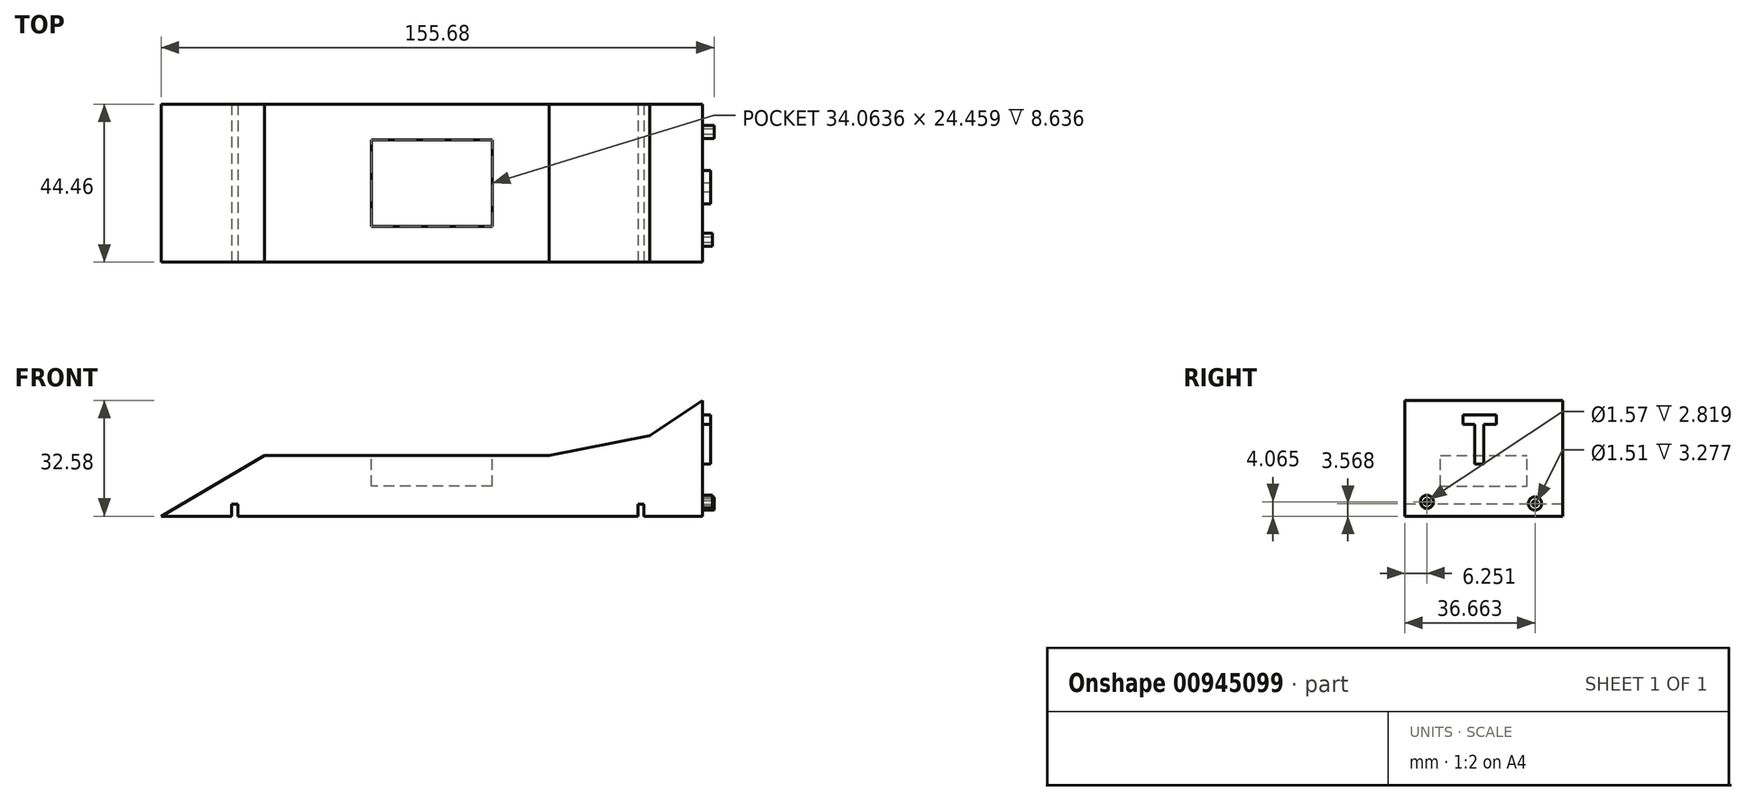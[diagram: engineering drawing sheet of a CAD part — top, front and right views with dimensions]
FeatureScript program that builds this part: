
annotation { "Feature Type Name" : "Feature", "Feature Type Description" : "" }
export const myFeature = defineFeature(function(context is Context, id is Id, definition is map)
    precondition{}
    {
        {
            var Q0;
            Q0=qCreatedBy(makeId("Top.planeOp"),FACE);
            var sketch = newSketch(context, id + "F0", { "sketchPlane" : qUnion([Q0])});
            skLineSegment(sketch, "E0.bottom", {"start": v(76.2, -22.22) * mm, "end": v(-76.2, -22.23) * mm});
            skLineSegment(sketch, "E0.top", {"start": v(76.2, 22.23) * mm, "end": v(-76.2, 22.22) * mm});
            skLineSegment(sketch, "E0.left", {"start": v(76.2, -22.22) * mm, "end": v(76.2, 22.23) * mm});
            skLineSegment(sketch, "E0.right", {"start": v(-76.2, -22.23) * mm, "end": v(-76.2, 22.22) * mm});
            skPoint(sketch, "E0.middle", {"position": v(0, 0) * mm});
            skSolve(sketch);
        }
        {
            var Q0;
            Q0 = qSketchRegion(id + "F0", true);
            extrude(context, id + "F1", {"entities" : qUnion([Q0]), "depth" : 38.1 * mm, "offsetDistance" : 25.4 * mm});
        }
        {
            var Q0;
            Q0=makeQuery(id+"F1.opExtrude","SWEPT_FACE",FACE,{"disambiguationData":[OSD([sQuery(id+"F0.wireOp",EDGE,"E0.bottom")])]});
            var sketch = newSketch(context, id + "F2", { "sketchPlane" : qUnion([Q0])});
            skLineSegment(sketch, "E1", {"start": v(-76.2, 0) * mm, "end": v(-47.13, 17.13) * mm});
            skLineSegment(sketch, "E2", {"start": v(-47.13, 17.13) * mm, "end": v(33.07, 17.13) * mm});
            skLineSegment(sketch, "E3", {"start": v(33.07, 17.13) * mm, "end": v(61.4, 22.68) * mm});
            skLineSegment(sketch, "E4", {"start": v(61.4, 22.68) * mm, "end": v(76.2, 32.58) * mm});
            skLineSegment(sketch, "E5", {"start": v(76.2, 32.58) * mm, "end": v(86.74, 41.3) * mm});
            skLineSegment(sketch, "E6", {"start": v(86.74, 41.3) * mm, "end": v(-31.3, 57.73) * mm});
            skLineSegment(sketch, "E7", {"start": v(-31.3, 57.73) * mm, "end": v(-92.1, 33.96) * mm});
            skLineSegment(sketch, "E8", {"start": v(-92.1, 33.96) * mm, "end": v(-76.2, 0) * mm});
            skSolve(sketch);
        }
        {
            var Q0;
            Q0 = qSketchRegion(id + "F2", true);
            extrude(context, id + "F3", {"entities" : qUnion([Q0]), "operationType" : NewBodyOperationType.REMOVE, "oppositeDirection" : true, "depth" : 87.38 * mm, "offsetDistance" : 25.4 * mm});
        }
        {
            var Q0;
            Q0=makeQuery(id+"F3.boolean.opBoolean","COPY",FACE,{"derivedFrom":makeQuery(id+"F3.opExtrude","SWEPT_FACE",FACE,{"disambiguationData":[OSD([sQuery(id+"F2.wireOp",EDGE,"E2")])]})});
            var sketch = newSketch(context, id + "F4", { "sketchPlane" : qUnion([Q0])});
            skLineSegment(sketch, "E9.bottom", {"start": v(17.03, -12.23) * mm, "end": v(-17.03, -12.23) * mm});
            skLineSegment(sketch, "E9.top", {"start": v(17.03, 12.23) * mm, "end": v(-17.03, 12.23) * mm});
            skLineSegment(sketch, "E9.left", {"start": v(17.03, -12.23) * mm, "end": v(17.03, 12.23) * mm});
            skLineSegment(sketch, "E9.right", {"start": v(-17.03, -12.23) * mm, "end": v(-17.03, 12.23) * mm});
            skPoint(sketch, "E9.middle", {"position": v(0, 0) * mm});
            skSolve(sketch);
        }
        {
            var Q0;
            Q0 = qSketchRegion(id + "F4", true);
            extrude(context, id + "F5", {"entities" : qUnion([Q0]), "operationType" : NewBodyOperationType.REMOVE, "oppositeDirection" : true, "depth" : 8.64 * mm, "offsetDistance" : 25.4 * mm});
        }
        {
            var Q0;
            Q0=makeQuery(id+"F1.opExtrude","SWEPT_FACE",FACE,{"disambiguationData":[OSD([sQuery(id+"F0.wireOp",EDGE,"E0.bottom")])]});
            var sketch = newSketch(context, id + "F6", { "sketchPlane" : qUnion([Q0])});
            skLineSegment(sketch, "E10.bottom", {"start": v(-56.32, 3.35) * mm, "end": v(-54.56, 3.35) * mm});
            skLineSegment(sketch, "E10.top", {"start": v(-56.32, -9.1) * mm, "end": v(-54.56, -9.1) * mm});
            skLineSegment(sketch, "E10.left", {"start": v(-56.32, 3.35) * mm, "end": v(-56.32, -9.1) * mm});
            skLineSegment(sketch, "E10.right", {"start": v(-54.56, 3.35) * mm, "end": v(-54.56, -9.1) * mm});
            skSolve(sketch);
        }
        {
            var Q0;
            Q0 = qSketchRegion(id + "F6", true);
            extrude(context, id + "F7", {"entities" : qUnion([Q0]), "operationType" : NewBodyOperationType.REMOVE, "oppositeDirection" : true, "depth" : 71.12 * mm, "offsetDistance" : 25.4 * mm});
        }
        {
            var Q0;
            Q0=makeQuery(id+"F1.opExtrude","SWEPT_FACE",FACE,{"disambiguationData":[OSD([sQuery(id+"F0.wireOp",EDGE,"E0.bottom")])]});
            var sketch = newSketch(context, id + "F8", { "sketchPlane" : qUnion([Q0])});
            skLineSegment(sketch, "E11.bottom", {"start": v(58.03, 3.35) * mm, "end": v(59.78, 3.35) * mm});
            skLineSegment(sketch, "E11.top", {"start": v(58.03, -2.18) * mm, "end": v(59.78, -2.18) * mm});
            skLineSegment(sketch, "E11.left", {"start": v(58.03, 3.35) * mm, "end": v(58.03, -2.18) * mm});
            skLineSegment(sketch, "E11.right", {"start": v(59.78, 3.35) * mm, "end": v(59.78, -2.18) * mm});
            skSolve(sketch);
        }
        {
            var Q0;
            Q0 = qSketchRegion(id + "F8", true);
            extrude(context, id + "F9", {"entities" : qUnion([Q0]), "operationType" : NewBodyOperationType.REMOVE, "oppositeDirection" : true, "depth" : 63.3 * mm, "offsetDistance" : 25.4 * mm});
        }
        {
            var Q0;
            Q0=makeQuery(id+"F1.opExtrude","SWEPT_FACE",FACE,{"disambiguationData":[OSD([sQuery(id+"F0.wireOp",EDGE,"E0.left")])]});
            var sketch = newSketch(context, id + "F10", { "sketchPlane" : qUnion([Q0])});
            skCircle(sketch, "E12", {"center": v(-15.98, 4.07) * mm, "radius": 0.78 * mm});
            skCircle(sketch, "E13", {"center": v(-15.98, 4.07) * mm, "radius": 1.85 * mm});
            skSolve(sketch);
        }
        {
            var Q0;
            Q0 = qSketchRegion(id + "F10", true);
            extrude(context, id + "F11", {"entities" : qUnion([Q0]), "operationType" : NewBodyOperationType.ADD, "depth" : 2.82 * mm, "offsetDistance" : 25.4 * mm});
        }
        {
            var Q0;
            {var subQ1=sQuery(id+"F0.wireOp",EDGE,"E0.left");var subQ2=sQuery(id+"F0.wireOp",EDGE,"E0.bottom");Q0=makeQuery(id+"F11.boolean.opBoolean","SPLIT",FACE,{"disambiguationData":[TD([makeQuery(id+"F1.opExtrude","SWEPT_FACE",FACE,{"disambiguationData":[OSD([subQ2])]})])],"derivedFrom":makeQuery(id+"F1.opExtrude","SWEPT_FACE",FACE,{"disambiguationData":[OSD([subQ1])]})});}
            var sketch = newSketch(context, id + "F12", { "sketchPlane" : qUnion([Q0])});
            skCircle(sketch, "E14", {"center": v(14.43, 3.57) * mm, "radius": 0.76 * mm});
            skCircle(sketch, "E15", {"center": v(14.43, 3.57) * mm, "radius": 1.87 * mm});
            skSolve(sketch);
        }
        {
            var Q0;
            Q0 = qSketchRegion(id + "F12", true);
            extrude(context, id + "F13", {"entities" : qUnion([Q0]), "operationType" : NewBodyOperationType.ADD, "depth" : 3.28 * mm, "offsetDistance" : 25.4 * mm});
        }
        {
            var Q0;
            {var subQ4=sQuery(id+"F0.wireOp",EDGE,"E0.left");var subQ5=sQuery(id+"F0.wireOp",EDGE,"E0.bottom");var subQ7=makeQuery(id+"F1.opExtrude","SWEPT_FACE",FACE,{"disambiguationData":[OSD([subQ5])]});Q0=makeQuery(id+"F13.boolean.opBoolean","SPLIT",FACE,{"disambiguationData":[TD([subQ7])],"derivedFrom":makeQuery(id+"F11.boolean.opBoolean","SPLIT",FACE,{"disambiguationData":[TD([subQ7])],"derivedFrom":makeQuery(id+"F1.opExtrude","SWEPT_FACE",FACE,{"disambiguationData":[OSD([subQ4])]})})});}
            var sketch = newSketch(context, id + "F14", { "sketchPlane" : qUnion([Q0])});
            skLineSegment(sketch, "E16.bottom", {"start": v(-2.56, 25.84) * mm, "end": v(0, 25.84) * mm});
            skLineSegment(sketch, "E16.top", {"start": v(-2.56, 14.73) * mm, "end": v(0, 14.73) * mm});
            skLineSegment(sketch, "E16.left", {"start": v(-2.56, 25.84) * mm, "end": v(-2.56, 14.73) * mm});
            skLineSegment(sketch, "E16.right", {"start": v(0, 25.84) * mm, "end": v(0, 14.73) * mm});
            skLineSegment(sketch, "E17.bottom", {"start": v(-5.87, 25.84) * mm, "end": v(3.52, 25.84) * mm});
            skLineSegment(sketch, "E17.top", {"start": v(-5.87, 28.53) * mm, "end": v(3.52, 28.53) * mm});
            skLineSegment(sketch, "E17.left", {"start": v(-5.87, 25.84) * mm, "end": v(-5.87, 28.53) * mm});
            skLineSegment(sketch, "E17.right", {"start": v(3.52, 25.84) * mm, "end": v(3.52, 28.53) * mm});
            skSolve(sketch);
        }
        {
            var Q0;
            Q0 = qSketchRegion(id + "F14", true);
            extrude(context, id + "F15", {"entities" : qUnion([Q0]), "operationType" : NewBodyOperationType.ADD, "depth" : 2.3 * mm, "offsetDistance" : 25.4 * mm});
        }
    });
